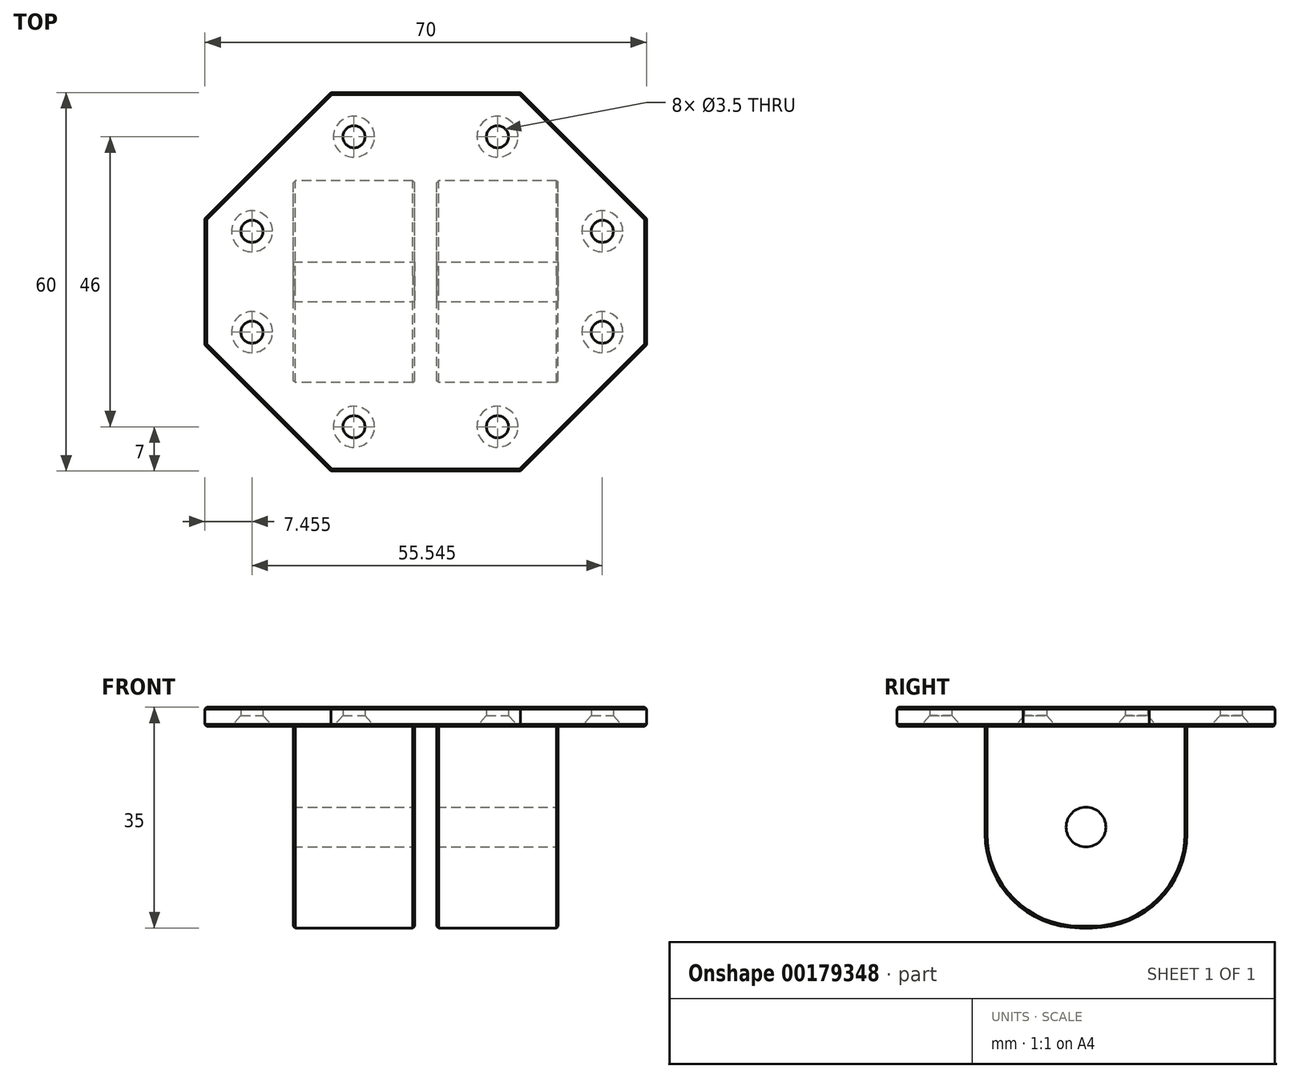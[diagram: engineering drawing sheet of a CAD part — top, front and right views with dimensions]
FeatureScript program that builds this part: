
annotation { "Feature Type Name" : "Feature", "Feature Type Description" : "" }
export const myFeature = defineFeature(function(context is Context, id is Id, definition is map)
    precondition{}
    {
        {
            var Q0;
            Q0=qCreatedBy(makeId("Top.planeOp"),FACE);
            var sketch = newSketch(context, id + "F0", { "sketchPlane" : qUnion([Q0])});
            skLineSegment(sketch, "E0.bottom", {"start": v(35, 30) * mm, "end": v(-35, 30) * mm});
            skLineSegment(sketch, "E0.top", {"start": v(35, -30) * mm, "end": v(-35, -30) * mm});
            skLineSegment(sketch, "E0.left", {"start": v(35, 30) * mm, "end": v(35, -30) * mm});
            skLineSegment(sketch, "E0.right", {"start": v(-35, 30) * mm, "end": v(-35, -30) * mm});
            skPoint(sketch, "E0.middle", {"position": v(0, 0) * mm});
            skLineSegment(sketch, "E1.bottom", {"start": v(21, -16) * mm, "end": v(1.75, -16) * mm});
            skLineSegment(sketch, "E1.top", {"start": v(21, 16) * mm, "end": v(1.75, 16) * mm});
            skLineSegment(sketch, "E1.left", {"start": v(21, -16) * mm, "end": v(21, 16) * mm});
            skLineSegment(sketch, "E1.right", {"start": v(-21, -16) * mm, "end": v(-21, 16) * mm});
            skLineSegment(sketch, "E2.left", {"start": v(1.75, -16) * mm, "end": v(1.75, 16) * mm});
            skLineSegment(sketch, "E2.right", {"start": v(-1.75, -16) * mm, "end": v(-1.75, 16) * mm});
            skLineSegment(sketch, "E3.trimOffspring", {"start": v(-1.75, -16) * mm, "end": v(-21, -16) * mm});
            skLineSegment(sketch, "E4.trimOffspring", {"start": v(-1.75, 16) * mm, "end": v(-21, 16) * mm});
            skLineSegment(sketch, "E5", {"start": v(11.38, 16) * mm, "end": v(11.38, 23) * mm, "construction": true});
            skLineSegment(sketch, "E6", {"start": v(-11.38, 16) * mm, "end": v(-11.38, 23) * mm, "construction": true});
            skLineSegment(sketch, "E7", {"start": v(11.38, -16) * mm, "end": v(11.38, -23) * mm, "construction": true});
            skLineSegment(sketch, "E8", {"start": v(-11.38, -16) * mm, "end": v(-11.38, -23) * mm, "construction": true});
            skLineSegment(sketch, "E9", {"start": v(-21, 0) * mm, "end": v(-27.54, 0) * mm, "construction": true});
            skPoint(sketch, "E9.endSnap0", {"position": v(-21, 0) * mm});
            skLineSegment(sketch, "E10", {"start": v(-27.54, -8) * mm, "end": v(-27.54, 8) * mm, "construction": true});
            skLineSegment(sketch, "E11", {"start": v(21, 0) * mm, "end": v(28, 0) * mm, "construction": true});
            skPoint(sketch, "E11.endSnap0", {"position": v(21, 0) * mm});
            skLineSegment(sketch, "E12", {"start": v(28, -8) * mm, "end": v(28, 8) * mm, "construction": true});
            skSolve(sketch);
        }
        {
            var Q0;
            {var subQ0=sQuery(id+"F0.wireOp",EDGE,"E1.left");Q0=makeQuery(id+"F0.imprint","IMPRINT",FACE,{"disambiguationData":[TD([[makeQuery(id+"F0.imprint","IMPRINT",EDGE,{"derivedFrom":subQ0}),1.0]])]});}
            var Q1;
            {var subQ0=sQuery(id+"F0.wireOp",EDGE,"E1.right");Q1=makeQuery(id+"F0.imprint","IMPRINT",FACE,{"disambiguationData":[TD([[makeQuery(id+"F0.imprint","IMPRINT",EDGE,{"derivedFrom":subQ0}),-1.0]])]});}
            var Q2;
            Q2=makeQuery(id+"F0.imprint","IMPRINT",FACE,{"disambiguationData":[TD([[makeQuery(id+"F0.imprint","IMPRINT",EDGE,{"derivedFrom":sQuery(id+"F0.wireOp",EDGE,"E0.bottom")}),1.0]])]});
            var Q3;
            Q3=makeQuery(id+"F0.imprint","IMPRINT",FACE,{"disambiguationData":[TD([[makeQuery(id+"F0.imprint","IMPRINT",EDGE,{"derivedFrom":sQuery(id+"F0.wireOp",EDGE,"E2.top")}),1.0]])]});
            extrude(context, id + "F1", {"entities" : qUnion([Q0, Q1, Q2, Q3]), "depth" : 3 * mm});
        }
        {
            var Q0;
            {var subQ0=sQuery(id+"F0.wireOp",EDGE,"E1.right");Q0=makeQuery(id+"F0.imprint","IMPRINT",FACE,{"disambiguationData":[TD([[makeQuery(id+"F0.imprint","IMPRINT",EDGE,{"derivedFrom":subQ0}),-1.0]])]});}
            var Q1;
            {var subQ0=sQuery(id+"F0.wireOp",EDGE,"E1.left");Q1=makeQuery(id+"F0.imprint","IMPRINT",FACE,{"disambiguationData":[TD([[makeQuery(id+"F0.imprint","IMPRINT",EDGE,{"derivedFrom":subQ0}),1.0]])]});}
            extrude(context, id + "F2", {"entities" : qUnion([Q0, Q1]), "operationType" : NewBodyOperationType.ADD, "oppositeDirection" : true, "depth" : 32 * mm});
        }
        {
            var Q0;
            Q0=makeQuery(id+"F2.opExtrude","SWEPT_FACE",FACE,{"disambiguationData":[OSD([sQuery(id+"F0.wireOp",EDGE,"E1.left")])]});
            var sketch = newSketch(context, id + "F3", { "sketchPlane" : qUnion([Q0])});
            skPoint(sketch, "E13", {"position": v(0, -16) * mm});
            skSolve(sketch);
        }
        {
            var Q0;
            Q0=sQuery(id+"F3.wireOp",VERTEX,"E13");
            var Q1;
            Q1=makeQuery(id+"F1.opExtrude","SWEPT_BODY",BODY,{"disambiguationData":[OSD([sQuery(id+"F0.wireOp",EDGE,"E0.bottom"),sQuery(id+"F0.wireOp",EDGE,"E0.top"),sQuery(id+"F0.wireOp",EDGE,"E0.left"),sQuery(id+"F0.wireOp",EDGE,"E0.right")])]});
            hole(context, id + "F4", {"style" : HoleStyle.SIMPLE, "endStyle" : HoleEndStyle.THROUGH, "holeDiameter" : 6.3 * mm, "locations" : qUnion([Q0]), "scope" : qUnion([Q1]), "isTappedThrough" : true});
        }
        {
            var Q0;
            Q0=makeQuery(id+"F2.opExtrude","CAP_EDGE",EDGE,{"disambiguationData":[OSD([sQuery(id+"F0.wireOp",EDGE,"E1.top")])],"isStart":false});
            var Q1;
            Q1=makeQuery(id+"F2.opExtrude","CAP_EDGE",EDGE,{"disambiguationData":[OSD([sQuery(id+"F0.wireOp",EDGE,"E1.bottom")])],"isStart":false});
            var Q2;
            Q2=makeQuery(id+"F2.opExtrude","CAP_EDGE",EDGE,{"disambiguationData":[OSD([sQuery(id+"F0.wireOp",EDGE,"E3.trimOffspring")])],"isStart":false});
            var Q3;
            Q3=makeQuery(id+"F2.opExtrude","CAP_EDGE",EDGE,{"disambiguationData":[OSD([sQuery(id+"F0.wireOp",EDGE,"E4.trimOffspring")])],"isStart":false});
            fillet(context, id + "F5", {"entities" : qUnion([Q0, Q1, Q2, Q3]), "radius" : 15 * mm, "tangentPropagation" : true, "allowEdgeOverflow" : false});
        }
        {
            var Q0;
            Q0=makeQuery(id+"F1.opExtrude","SWEPT_EDGE",EDGE,{"disambiguationData":[OSD([sQuery(id+"F0.wireOp",EDGE,"E0.bottom"),sQuery(id+"F0.wireOp",EDGE,"E0.right")])]});
            var Q1;
            Q1=makeQuery(id+"F1.opExtrude","SWEPT_EDGE",EDGE,{"disambiguationData":[OSD([sQuery(id+"F0.wireOp",EDGE,"E0.top"),sQuery(id+"F0.wireOp",EDGE,"E0.right")])]});
            var Q2;
            Q2=makeQuery(id+"F1.opExtrude","SWEPT_EDGE",EDGE,{"disambiguationData":[OSD([sQuery(id+"F0.wireOp",EDGE,"E0.top"),sQuery(id+"F0.wireOp",EDGE,"E0.left")])]});
            var Q3;
            Q3=makeQuery(id+"F1.opExtrude","SWEPT_EDGE",EDGE,{"disambiguationData":[OSD([sQuery(id+"F0.wireOp",EDGE,"E0.bottom"),sQuery(id+"F0.wireOp",EDGE,"E0.left")])]});
            chamfer(context, id + "F6", {"entities" : qUnion([Q0, Q1, Q2, Q3]), "width" : 20 * mm, "tangentPropagation" : true});
        }
        {
            var Q0;
            Q0=sQuery(id+"F0.wireOp",VERTEX,"E6.end");
            var Q1;
            Q1=sQuery(id+"F0.wireOp",VERTEX,"E5.end");
            var Q2;
            Q2=sQuery(id+"F0.wireOp",VERTEX,"E12.end");
            var Q3;
            Q3=sQuery(id+"F0.wireOp",VERTEX,"E12.start");
            var Q4;
            Q4=sQuery(id+"F0.wireOp",VERTEX,"E7.end");
            var Q5;
            Q5=sQuery(id+"F0.wireOp",VERTEX,"E8.end");
            var Q6;
            Q6=sQuery(id+"F0.wireOp",VERTEX,"E10.start");
            var Q7;
            Q7=sQuery(id+"F0.wireOp",VERTEX,"E10.end");
            var Q8;
            Q8=makeQuery(id+"F1.opExtrude","SWEPT_BODY",BODY,{"disambiguationData":[OSD([sQuery(id+"F0.wireOp",EDGE,"E0.bottom"),sQuery(id+"F0.wireOp",EDGE,"E0.top"),sQuery(id+"F0.wireOp",EDGE,"E0.left"),sQuery(id+"F0.wireOp",EDGE,"E0.right")])]});
            hole(context, id + "F7", {"style" : HoleStyle.C_SINK, "endStyle" : HoleEndStyle.THROUGH, "oppositeDirection" : true, "holeDiameter" : 3.5 * mm, "cSinkDiameter" : 6.5 * mm, "cSinkAngle" : 82 * degree, "locations" : qUnion([Q0, Q1, Q2, Q3, Q4, Q5, Q6, Q7]), "scope" : qUnion([Q8]), "isTappedThrough" : true});
        }
        {
            var Q0;
            Q0=makeQuery(id+"F2.opExtrude","SWEPT_EDGE",EDGE,{"disambiguationData":[OSD([sQuery(id+"F0.wireOp",EDGE,"E1.bottom"),sQuery(id+"F0.wireOp",EDGE,"E1.right")])]});
            var Q1;
            Q1=makeQuery(id+"F2.opExtrude","SWEPT_EDGE",EDGE,{"disambiguationData":[OSD([sQuery(id+"F0.wireOp",EDGE,"E1.bottom"),sQuery(id+"F0.wireOp",EDGE,"E2.right")])]});
            var Q2;
            Q2=makeQuery(id+"F2.opExtrude","SWEPT_EDGE",EDGE,{"disambiguationData":[OSD([sQuery(id+"F0.wireOp",EDGE,"E1.bottom"),sQuery(id+"F0.wireOp",EDGE,"E2.left")])]});
            var Q3;
            Q3=makeQuery(id+"F2.opExtrude","SWEPT_EDGE",EDGE,{"disambiguationData":[OSD([sQuery(id+"F0.wireOp",EDGE,"E1.bottom"),sQuery(id+"F0.wireOp",EDGE,"E1.left")])]});
            var Q4;
            Q4=makeQuery(id+"F1.opExtrude","CAP_EDGE",EDGE,{"disambiguationData":[OSD([sQuery(id+"F0.wireOp",EDGE,"E0.top")])],"isStart":true});
            var Q5;
            Q5=makeQuery(id+"F1.opExtrude","CAP_EDGE",EDGE,{"disambiguationData":[OSD([sQuery(id+"F0.wireOp",EDGE,"E0.left")])],"isStart":true});
            var Q6;
            Q6=makeQuery(id+"F1.opExtrude","CAP_EDGE",EDGE,{"disambiguationData":[OSD([sQuery(id+"F0.wireOp",EDGE,"E0.top")])],"isStart":false});
            var Q7;
            Q7=makeQuery(id+"F1.opExtrude","CAP_EDGE",EDGE,{"disambiguationData":[OSD([sQuery(id+"F0.wireOp",EDGE,"E0.left")])],"isStart":false});
            var Q8;
            Q8=makeQuery(id+"F1.opExtrude","CAP_EDGE",EDGE,{"disambiguationData":[OSD([sQuery(id+"F0.wireOp",EDGE,"E0.bottom")])],"isStart":false});
            var Q9;
            Q9=makeQuery(id+"F1.opExtrude","CAP_EDGE",EDGE,{"disambiguationData":[OSD([sQuery(id+"F0.wireOp",EDGE,"E0.bottom")])],"isStart":true});
            var Q10;
            Q10=makeQuery(id+"F1.opExtrude","CAP_EDGE",EDGE,{"disambiguationData":[OSD([sQuery(id+"F0.wireOp",EDGE,"E0.right")])],"isStart":false});
            var Q11;
            Q11=makeQuery(id+"F1.opExtrude","CAP_EDGE",EDGE,{"disambiguationData":[OSD([sQuery(id+"F0.wireOp",EDGE,"E0.right")])],"isStart":true});
            var Q12;
            Q12=makeQuery(id+"F4.hole-0.boolean.opBoolean","COPY",EDGE,{"derivedFrom":makeQuery(id+"F4.hole-0.opRevolve","SWEPT_EDGE",EDGE,{"disambiguationData":[OSD([sQuery(id+"F4.hole-0.sketch.wireOp",EDGE,"core_line_2"),sQuery(id+"F4.hole-0.sketch.wireOp",EDGE,"core_line_3")])]})});
            var Q13;
            Q13=makeQuery(id+"F4.hole-0.boolean.opBoolean","INTERSECT",EDGE,{"derivedFrom":[makeQuery(id+"F2.opExtrude","SWEPT_FACE",FACE,{"disambiguationData":[OSD([sQuery(id+"F0.wireOp",EDGE,"E2.left")])]}),makeQuery(id+"F4.hole-0.opRevolve","SWEPT_FACE",FACE,{"disambiguationData":[OSD([sQuery(id+"F4.hole-0.sketch.wireOp",EDGE,"core_line_2")])]})]});
            var Q14;
            Q14=makeQuery(id+"F4.hole-0.boolean.opBoolean","INTERSECT",EDGE,{"derivedFrom":[makeQuery(id+"F2.opExtrude","SWEPT_FACE",FACE,{"disambiguationData":[OSD([sQuery(id+"F0.wireOp",EDGE,"E2.right")])]}),makeQuery(id+"F4.hole-0.opRevolve","SWEPT_FACE",FACE,{"disambiguationData":[OSD([sQuery(id+"F4.hole-0.sketch.wireOp",EDGE,"core_line_2")])]})]});
            var Q15;
            Q15=makeQuery(id+"F4.hole-0.boolean.opBoolean","INTERSECT",EDGE,{"derivedFrom":[makeQuery(id+"F2.opExtrude","SWEPT_FACE",FACE,{"disambiguationData":[OSD([sQuery(id+"F0.wireOp",EDGE,"E1.right")])]}),makeQuery(id+"F4.hole-0.opRevolve","SWEPT_FACE",FACE,{"disambiguationData":[OSD([sQuery(id+"F4.hole-0.sketch.wireOp",EDGE,"core_line_2")])]})]});
            var Q16;
            {var subQ0=sQuery(id+"F0.wireOp",EDGE,"E0.right");var subQ1=sQuery(id+"F0.wireOp",EDGE,"E0.top");Q16=makeQuery(id+"F6.opChamfer","BLEND_EDGE",EDGE,{"blendedFrom":[makeQuery(id+"F1.opExtrude","SWEPT_EDGE",EDGE,{"disambiguationData":[OSD([subQ1,subQ0])]}),makeQuery(id+"F1.opExtrude","CAP_FACE",FACE,{"disambiguationData":[OSD([sQuery(id+"F0.wireOp",EDGE,"E0.bottom"),subQ1,sQuery(id+"F0.wireOp",EDGE,"E0.left"),subQ0])],"isStart":true})],"blendedInto":[makeQuery(id+"F1.opExtrude","CAP_FACE",FACE,{"disambiguationData":[OSD([sQuery(id+"F0.wireOp",EDGE,"E0.bottom"),subQ1,sQuery(id+"F0.wireOp",EDGE,"E0.left"),subQ0])],"isStart":true})]});}
            var Q17;
            {var subQ0=sQuery(id+"F0.wireOp",EDGE,"E0.right");var subQ1=sQuery(id+"F0.wireOp",EDGE,"E0.top");Q17=makeQuery(id+"F6.opChamfer","BLEND_EDGE",EDGE,{"blendedFrom":[makeQuery(id+"F1.opExtrude","SWEPT_EDGE",EDGE,{"disambiguationData":[OSD([subQ1,subQ0])]}),makeQuery(id+"F1.opExtrude","CAP_FACE",FACE,{"disambiguationData":[OSD([sQuery(id+"F0.wireOp",EDGE,"E0.bottom"),subQ1,sQuery(id+"F0.wireOp",EDGE,"E0.left"),subQ0])],"isStart":false})],"blendedInto":[makeQuery(id+"F1.opExtrude","CAP_FACE",FACE,{"disambiguationData":[OSD([sQuery(id+"F0.wireOp",EDGE,"E0.bottom"),subQ1,sQuery(id+"F0.wireOp",EDGE,"E0.left"),subQ0])],"isStart":false})]});}
            var Q18;
            {var subQ0=sQuery(id+"F0.wireOp",EDGE,"E0.right");var subQ1=sQuery(id+"F0.wireOp",EDGE,"E0.bottom");Q18=makeQuery(id+"F6.opChamfer","BLEND_EDGE",EDGE,{"blendedFrom":[makeQuery(id+"F1.opExtrude","SWEPT_EDGE",EDGE,{"disambiguationData":[OSD([subQ1,subQ0])]}),makeQuery(id+"F1.opExtrude","CAP_FACE",FACE,{"disambiguationData":[OSD([subQ1,sQuery(id+"F0.wireOp",EDGE,"E0.top"),sQuery(id+"F0.wireOp",EDGE,"E0.left"),subQ0])],"isStart":true})],"blendedInto":[makeQuery(id+"F1.opExtrude","CAP_FACE",FACE,{"disambiguationData":[OSD([subQ1,sQuery(id+"F0.wireOp",EDGE,"E0.top"),sQuery(id+"F0.wireOp",EDGE,"E0.left"),subQ0])],"isStart":true})]});}
            var Q19;
            {var subQ0=sQuery(id+"F0.wireOp",EDGE,"E0.right");var subQ1=sQuery(id+"F0.wireOp",EDGE,"E0.bottom");Q19=makeQuery(id+"F6.opChamfer","BLEND_EDGE",EDGE,{"blendedFrom":[makeQuery(id+"F1.opExtrude","SWEPT_EDGE",EDGE,{"disambiguationData":[OSD([subQ1,subQ0])]}),makeQuery(id+"F1.opExtrude","CAP_FACE",FACE,{"disambiguationData":[OSD([subQ1,sQuery(id+"F0.wireOp",EDGE,"E0.top"),sQuery(id+"F0.wireOp",EDGE,"E0.left"),subQ0])],"isStart":false})],"blendedInto":[makeQuery(id+"F1.opExtrude","CAP_FACE",FACE,{"disambiguationData":[OSD([subQ1,sQuery(id+"F0.wireOp",EDGE,"E0.top"),sQuery(id+"F0.wireOp",EDGE,"E0.left"),subQ0])],"isStart":false})]});}
            var Q20;
            {var subQ0=sQuery(id+"F0.wireOp",EDGE,"E0.left");var subQ1=sQuery(id+"F0.wireOp",EDGE,"E0.bottom");Q20=makeQuery(id+"F6.opChamfer","BLEND_EDGE",EDGE,{"blendedFrom":[makeQuery(id+"F1.opExtrude","SWEPT_EDGE",EDGE,{"disambiguationData":[OSD([subQ1,subQ0])]}),makeQuery(id+"F1.opExtrude","CAP_FACE",FACE,{"disambiguationData":[OSD([subQ1,sQuery(id+"F0.wireOp",EDGE,"E0.top"),subQ0,sQuery(id+"F0.wireOp",EDGE,"E0.right")])],"isStart":false})],"blendedInto":[makeQuery(id+"F1.opExtrude","CAP_FACE",FACE,{"disambiguationData":[OSD([subQ1,sQuery(id+"F0.wireOp",EDGE,"E0.top"),subQ0,sQuery(id+"F0.wireOp",EDGE,"E0.right")])],"isStart":false})]});}
            var Q21;
            {var subQ0=sQuery(id+"F0.wireOp",EDGE,"E0.left");var subQ1=sQuery(id+"F0.wireOp",EDGE,"E0.bottom");Q21=makeQuery(id+"F6.opChamfer","BLEND_EDGE",EDGE,{"blendedFrom":[makeQuery(id+"F1.opExtrude","SWEPT_EDGE",EDGE,{"disambiguationData":[OSD([subQ1,subQ0])]}),makeQuery(id+"F1.opExtrude","CAP_FACE",FACE,{"disambiguationData":[OSD([subQ1,sQuery(id+"F0.wireOp",EDGE,"E0.top"),subQ0,sQuery(id+"F0.wireOp",EDGE,"E0.right")])],"isStart":true})],"blendedInto":[makeQuery(id+"F1.opExtrude","CAP_FACE",FACE,{"disambiguationData":[OSD([subQ1,sQuery(id+"F0.wireOp",EDGE,"E0.top"),subQ0,sQuery(id+"F0.wireOp",EDGE,"E0.right")])],"isStart":true})]});}
            var Q22;
            {var subQ0=sQuery(id+"F0.wireOp",EDGE,"E0.left");var subQ1=sQuery(id+"F0.wireOp",EDGE,"E0.top");Q22=makeQuery(id+"F6.opChamfer","BLEND_EDGE",EDGE,{"blendedFrom":[makeQuery(id+"F1.opExtrude","SWEPT_EDGE",EDGE,{"disambiguationData":[OSD([subQ1,subQ0])]}),makeQuery(id+"F1.opExtrude","CAP_FACE",FACE,{"disambiguationData":[OSD([sQuery(id+"F0.wireOp",EDGE,"E0.bottom"),subQ1,subQ0,sQuery(id+"F0.wireOp",EDGE,"E0.right")])],"isStart":false})],"blendedInto":[makeQuery(id+"F1.opExtrude","CAP_FACE",FACE,{"disambiguationData":[OSD([sQuery(id+"F0.wireOp",EDGE,"E0.bottom"),subQ1,subQ0,sQuery(id+"F0.wireOp",EDGE,"E0.right")])],"isStart":false})]});}
            var Q23;
            {var subQ0=sQuery(id+"F0.wireOp",EDGE,"E0.left");var subQ1=sQuery(id+"F0.wireOp",EDGE,"E0.top");Q23=makeQuery(id+"F6.opChamfer","BLEND_EDGE",EDGE,{"blendedFrom":[makeQuery(id+"F1.opExtrude","SWEPT_EDGE",EDGE,{"disambiguationData":[OSD([subQ1,subQ0])]}),makeQuery(id+"F1.opExtrude","CAP_FACE",FACE,{"disambiguationData":[OSD([sQuery(id+"F0.wireOp",EDGE,"E0.bottom"),subQ1,subQ0,sQuery(id+"F0.wireOp",EDGE,"E0.right")])],"isStart":true})],"blendedInto":[makeQuery(id+"F1.opExtrude","CAP_FACE",FACE,{"disambiguationData":[OSD([sQuery(id+"F0.wireOp",EDGE,"E0.bottom"),subQ1,subQ0,sQuery(id+"F0.wireOp",EDGE,"E0.right")])],"isStart":true})]});}
            chamfer(context, id + "F8", {"entities" : qUnion([Q0, Q1, Q2, Q3, Q4, Q5, Q6, Q7, Q8, Q9, Q10, Q11, Q12, Q13, Q14, Q15, Q16, Q17, Q18, Q19, Q20, Q21, Q22, Q23]), "width" : .3 * mm, "tangentPropagation" : true});
        }
    });
